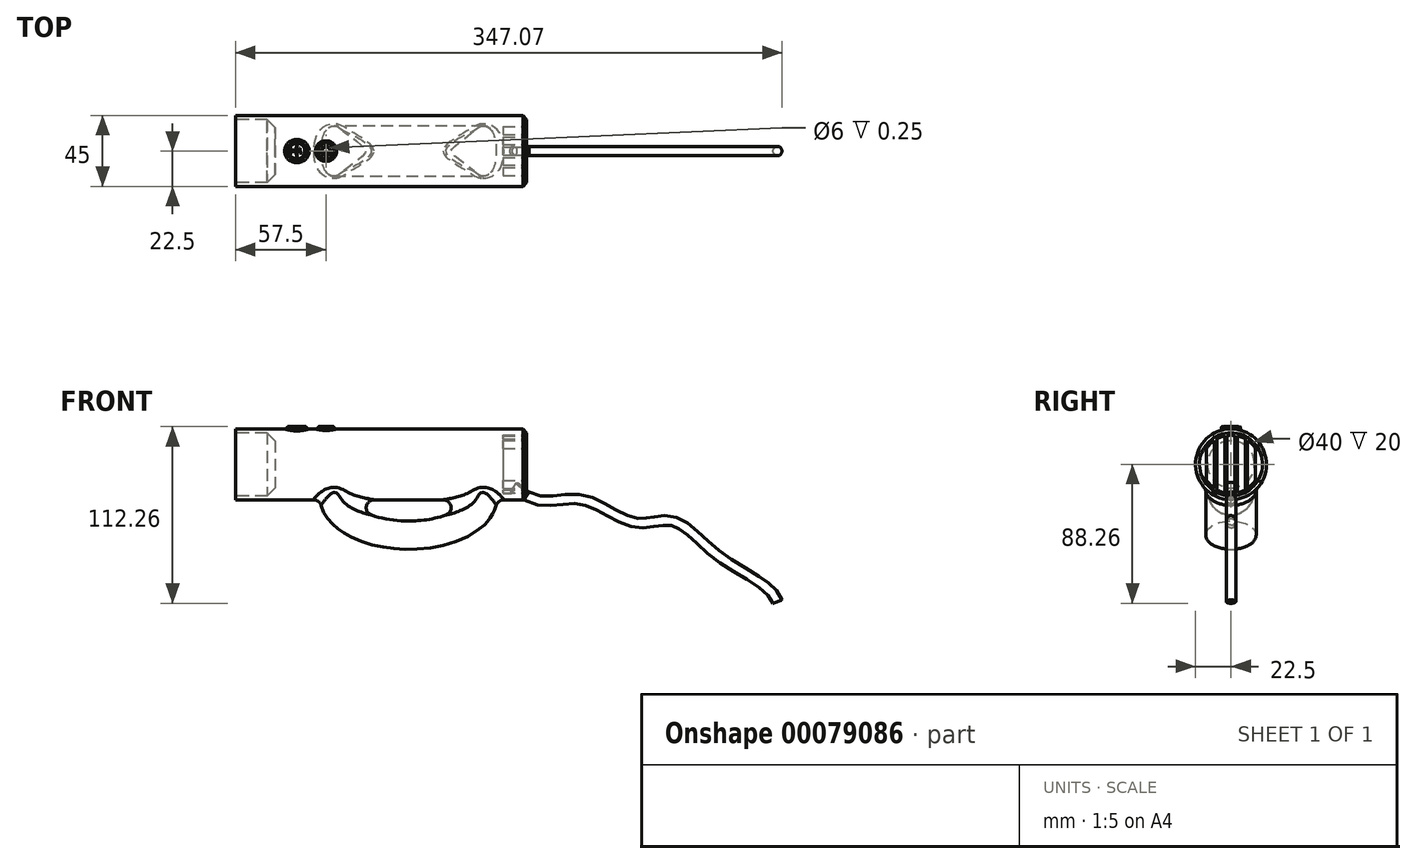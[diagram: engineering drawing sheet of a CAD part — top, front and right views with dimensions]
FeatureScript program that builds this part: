
annotation { "Feature Type Name" : "Feature", "Feature Type Description" : "" }
export const myFeature = defineFeature(function(context is Context, id is Id, definition is map)
    precondition{}
    {
        {
            var Q0;
            Q0=qCreatedBy(makeId("Front.planeOp"),FACE);
            var sketch = newSketch(context, id + "F0", { "sketchPlane" : qUnion([Q0])});
            skEllipse(sketch, "E0", {"center": v(0, -5) * mm, "majorRadius": 47.5 * mm, "minorRadius": 25 * mm, "majorAxis": v(1, 0)});
            skSolve(sketch);
        }
        {
            var Q0;
            Q0=qCreatedBy(makeId("Right.planeOp"),FACE);
            var sketch = newSketch(context, id + "F1", { "sketchPlane" : qUnion([Q0])});
            skLineSegment(sketch, "E1.0", {"start": v(0, -30) * mm, "end": v(0, 20) * mm});
            skEllipse(sketch, "E2", {"center": v(0, -30) * mm, "majorRadius": 16 * mm, "minorRadius": 9 * mm, "majorAxis": v(-1, 0)});
            skSolve(sketch);
        }
        {
            var Q0;
            Q0=makeQuery(id+"F1.imprint","IMPRINT",FACE,{"disambiguationData":[TD([[makeQuery(id+"F1.imprint","IMPRINT",EDGE,{"derivedFrom":sQuery(id+"F1.wireOp",EDGE,"E2")}),1.0]])]});
            var Q1;
            Q1=sQuery(id+"F0.wireOp",EDGE,"E0");
            sweep(context, id + "F2", {"profiles" : qUnion([Q0]), "path" : qUnion([Q1])});
        }
        {
            var Q0;
            Q0=qCreatedBy(makeId("Right.planeOp"),FACE);
            var sketch = newSketch(context, id + "F3", { "sketchPlane" : qUnion([Q0])});
            skCircle(sketch, "E3", {"center": v(0, 15) * mm, "radius": 22.5 * mm});
            skSolve(sketch);
        }
        {
            var Q0;
            Q0=makeQuery(id+"F3.imprint","IMPRINT",FACE,{"disambiguationData":[TD([[makeQuery(id+"F3.imprint","IMPRINT",EDGE,{"derivedFrom":sQuery(id+"F3.wireOp",EDGE,"E3")}),1.0]])]});
            extrude(context, id + "F4", {"entities" : qUnion([Q0]), "depth" : 75 * mm, "hasSecondDirection" : true, "secondDirectionOppositeDirection" : true, "secondDirectionDepth" : 110 * mm});
        }
        {
            var Q0;
            Q0=makeQuery(id+"F4.opExtrude","CAP_FACE",FACE,{"disambiguationData":[OSD([sQuery(id+"F3.wireOp",EDGE,"E3")])],"isStart":true});
            var sketch = newSketch(context, id + "F5", { "sketchPlane" : qUnion([Q0])});
            skCircle(sketch, "E4", {"center": v(0, 15) * mm, "radius": 20 * mm});
            skSolve(sketch);
        }
        {
            var Q0;
            Q0=makeQuery(id+"F5.imprint","IMPRINT",FACE,{"disambiguationData":[TD([[makeQuery(id+"F5.imprint","IMPRINT",EDGE,{"derivedFrom":sQuery(id+"F5.wireOp",EDGE,"E4")}),1.0]])]});
            extrude(context, id + "F6", {"entities" : qUnion([Q0]), "operationType" : NewBodyOperationType.REMOVE, "oppositeDirection" : true, "depth" : 25 * mm});
        }
        {
            var Q0;
            Q0=makeQuery(id+"F4.opExtrude","SWEPT_BODY",BODY,{"disambiguationData":[OSD([sQuery(id+"F3.wireOp",EDGE,"E3")])]});
            var Q1;
            Q1=makeQuery(id+"F2.opSweep","SWEPT_BODY",BODY,{"disambiguationData":[OSD([sQuery(id+"F0.wireOp",EDGE,"E0"),sQuery(id+"F1.wireOp",EDGE,"E2")])]});
            booleanBodies(context, id + "F7", {"operationType" : BooleanOperationType.UNION, "tools" : qUnion([Q0, Q1])});
        }
        {
            var Q0;
            Q0=makeQuery(id+"F7.opBoolean","INTERSECT",EDGE,{"disambiguationData":[OD(0.0)],"derivedFrom":[makeQuery(id+"F2.opSweep","SWEPT_FACE",FACE,{"disambiguationData":[OSD([sQuery(id+"F0.wireOp",EDGE,"E0"),sQuery(id+"F1.wireOp",EDGE,"E2")])]}),makeQuery(id+"F4.opExtrude","SWEPT_FACE",FACE,{"disambiguationData":[OSD([sQuery(id+"F3.wireOp",EDGE,"E3")])]})]});
            var Q1;
            Q1=makeQuery(id+"F7.opBoolean","INTERSECT",EDGE,{"disambiguationData":[OD(1.0)],"derivedFrom":[makeQuery(id+"F2.opSweep","SWEPT_FACE",FACE,{"disambiguationData":[OSD([sQuery(id+"F0.wireOp",EDGE,"E0"),sQuery(id+"F1.wireOp",EDGE,"E2")])]}),makeQuery(id+"F4.opExtrude","SWEPT_FACE",FACE,{"disambiguationData":[OSD([sQuery(id+"F3.wireOp",EDGE,"E3")])]})]});
            fillet(context, id + "F8", {"entities" : qUnion([Q0, Q1]), "radius" : 5 * mm, "tangentPropagation" : true, "allowEdgeOverflow" : false});
        }
        {
            var Q0;
            Q0=makeQuery(id+"F4.opExtrude","CAP_EDGE",EDGE,{"disambiguationData":[OSD([sQuery(id+"F3.wireOp",EDGE,"E3")])],"isStart":false});
            chamfer(context, id + "F9", {"entities" : qUnion([Q0]), "width" : 2.5 * mm, "tangentPropagation" : true});
        }
        {
            var Q0;
            Q0=qCreatedBy(makeId("Top.planeOp"),FACE);
            var sketch = newSketch(context, id + "F10", { "sketchPlane" : qUnion([Q0])});
            skCircle(sketch, "E5", {"center": v(-52.5, 0) * mm, "radius": 5 * mm});
            skCircle(sketch, "E6", {"center": v(-71, 0) * mm, "radius": 6 * mm});
            skSolve(sketch);
        }
        {
            var Q0;
            Q0=makeQuery(id+"F10.imprint","IMPRINT",FACE,{"disambiguationData":[TD([[makeQuery(id+"F10.imprint","IMPRINT",EDGE,{"derivedFrom":sQuery(id+"F10.wireOp",EDGE,"E5")}),1.0]])]});
            var Q1;
            Q1=makeQuery(id+"F10.imprint","IMPRINT",FACE,{"disambiguationData":[TD([[makeQuery(id+"F10.imprint","IMPRINT",EDGE,{"derivedFrom":sQuery(id+"F10.wireOp",EDGE,"E6")}),1.0]])]});
            extrude(context, id + "F11", {"entities" : qUnion([Q0, Q1]), "depth" : 39 * mm, "hasSecondDirection" : true, "secondDirectionOppositeDirection" : false, "secondDirectionDepth" : 25 * mm});
        }
        {
            var Q0;
            Q0=makeQuery(id+"F11.opExtrude","CAP_EDGE",EDGE,{"disambiguationData":[OSD([sQuery(id+"F10.wireOp",EDGE,"E6")])],"isStart":false});
            var Q1;
            Q1=makeQuery(id+"F11.opExtrude","CAP_FACE",FACE,{"disambiguationData":[OSD([sQuery(id+"F10.wireOp",EDGE,"E5")])],"isStart":false});
            fillet(context, id + "F12", {"entities" : qUnion([Q0, Q1]), "radius" : 0.5 * mm, "tangentPropagation" : true, "allowEdgeOverflow" : false});
        }
        {
            var Q0;
            Q0=makeQuery(id+"F4.opExtrude","SWEPT_BODY",BODY,{"disambiguationData":[OSD([sQuery(id+"F3.wireOp",EDGE,"E3")])]});
            var Q1;
            Q1=makeQuery(id+"F11.opExtrude","SWEPT_BODY",BODY,{"disambiguationData":[OSD([sQuery(id+"F10.wireOp",EDGE,"E6")])]});
            var Q2;
            Q2=makeQuery(id+"F11.opExtrude","SWEPT_BODY",BODY,{"disambiguationData":[OSD([sQuery(id+"F10.wireOp",EDGE,"E5")])]});
            booleanBodies(context, id + "F13", {"operationType" : BooleanOperationType.UNION, "tools" : qUnion([Q0, Q1, Q2])});
        }
        {
            var Q0;
            Q0=makeQuery(id+"F13.opBoolean","INTERSECT",EDGE,{"derivedFrom":[makeQuery(id+"F4.opExtrude","SWEPT_FACE",FACE,{"disambiguationData":[OSD([sQuery(id+"F3.wireOp",EDGE,"E3")])]}),makeQuery(id+"F11.opExtrude","SWEPT_FACE",FACE,{"disambiguationData":[OSD([sQuery(id+"F10.wireOp",EDGE,"E6")])]})]});
            var Q1;
            Q1=makeQuery(id+"F13.opBoolean","INTERSECT",EDGE,{"derivedFrom":[makeQuery(id+"F4.opExtrude","SWEPT_FACE",FACE,{"disambiguationData":[OSD([sQuery(id+"F3.wireOp",EDGE,"E3")])]}),makeQuery(id+"F11.opExtrude","SWEPT_FACE",FACE,{"disambiguationData":[OSD([sQuery(id+"F10.wireOp",EDGE,"E5")])]})]});
            fillet(context, id + "F14", {"entities" : qUnion([Q0, Q1]), "radius" : 2 * mm, "tangentPropagation" : true, "allowEdgeOverflow" : false});
        }
        {
            var Q0;
            Q0=makeQuery(id+"F11.opExtrude","CAP_FACE",FACE,{"disambiguationData":[OSD([sQuery(id+"F10.wireOp",EDGE,"E5")])],"isStart":false});
            var sketch = newSketch(context, id + "F15", { "sketchPlane" : qUnion([Q0])});
            skCircle(sketch, "E7", {"center": v(-52.5, 0) * mm, "radius": 3 * mm});
            skCircle(sketch, "E8.0", {"center": v(-52.5, 0) * mm, "radius": 2.5 * mm});
            skLineSegment(sketch, "E9.bottom", {"start": v(-52.75, -2.75) * mm, "end": v(-52.25, -2.75) * mm});
            skLineSegment(sketch, "E9.top", {"start": v(-52.75, -0.75) * mm, "end": v(-52.25, -0.75) * mm});
            skLineSegment(sketch, "E9.left", {"start": v(-52.75, -2.75) * mm, "end": v(-52.75, -0.75) * mm});
            skLineSegment(sketch, "E9.right", {"start": v(-52.25, -2.75) * mm, "end": v(-52.25, -0.75) * mm});
            skSolve(sketch);
        }
        {
            var Q0;
            Q0=makeQuery(id+"F15.imprint","IMPRINT",FACE,{"disambiguationData":[TD([[makeQuery(id+"F15.imprint","IMPRINT",EDGE,{"derivedFrom":sQuery(id+"F15.wireOp",EDGE,"E7")}),1.0]])]});
            var Q1;
            {var subQ5=sQuery(id+"F15.wireOp",EDGE,"E9.top");Q1=makeQuery(id+"F15.imprint","IMPRINT",FACE,{"disambiguationData":[TD([[makeQuery(id+"F15.imprint","IMPRINT",EDGE,{"derivedFrom":subQ5}),-1.0]])]});}
            var Q2;
            {var subQ5=sQuery(id+"F15.wireOp",EDGE,"E9.bottom");Q2=makeQuery(id+"F15.imprint","IMPRINT",FACE,{"disambiguationData":[TD([[makeQuery(id+"F15.imprint","IMPRINT",EDGE,{"derivedFrom":subQ5}),1.0]])]});}
            extrude(context, id + "F16", {"entities" : qUnion([Q0, Q1, Q2]), "operationType" : NewBodyOperationType.REMOVE, "oppositeDirection" : true, "depth" : 0.25 * mm});
        }
        {
            var Q0;
            Q0=makeQuery(id+"F11.opExtrude","CAP_FACE",FACE,{"disambiguationData":[OSD([sQuery(id+"F10.wireOp",EDGE,"E6")])],"isStart":false});
            var sketch = newSketch(context, id + "F17", { "sketchPlane" : qUnion([Q0])});
            skCircle(sketch, "E10", {"center": v(-71, 0) * mm, "radius": 5.25 * mm});
            skCircle(sketch, "E11.0", {"center": v(-71, 0) * mm, "radius": 5 * mm});
            skLineSegment(sketch, "E12", {"start": v(-71.13, -5) * mm, "end": v(-71.13, 5) * mm});
            skLineSegment(sketch, "E13", {"start": v(-70.88, -5) * mm, "end": v(-70.88, 5) * mm});
            skText(sketch, "E14", { "text": "H", "fontName": "OpenSans-Regular.ttf"});
            skText(sketch, "E15", { "text": "L", "fontName": "OpenSans-Regular.ttf"});
            const initialGuessF17  = {"E14": [-0.07476, -0.00138, 1, 0, 0.00291], "E15": [-0.06985, -0.00138, 1, 0, 0.00325]};
            skSetInitialGuess(sketch, initialGuessF17);
            skSolve(sketch);
        }
        {
            var Q0;
            {var subQ0=sQuery(id+"F17.wireOp",EDGE,"E12");Q0=makeQuery(id+"F17.imprint","IMPRINT",FACE,{"disambiguationData":[TD([[makeQuery(id+"F17.imprint","IMPRINT",EDGE,{"derivedFrom":subQ0}),1.0]])]});}
            var Q1;
            {var subQ0=sQuery(id+"F17.wireOp",EDGE,"E13");Q1=makeQuery(id+"F17.imprint","IMPRINT",FACE,{"disambiguationData":[TD([[makeQuery(id+"F17.imprint","IMPRINT",EDGE,{"derivedFrom":subQ0}),-1.0]])]});}
            extrude(context, id + "F18", {"entities" : qUnion([Q0, Q1]), "operationType" : NewBodyOperationType.REMOVE, "oppositeDirection" : true, "depth" : 0.25 * mm});
        }
        {
            var Q0;
            Q0=makeQuery(id+"F6.boolean.opBoolean","COPY",EDGE,{"derivedFrom":makeQuery(id+"F6.opExtrude","CAP_EDGE",EDGE,{"disambiguationData":[OSD([sQuery(id+"F5.wireOp",EDGE,"E4")])],"isStart":false})});
            chamfer(context, id + "F19", {"entities" : qUnion([Q0]), "width" : 5 * mm, "tangentPropagation" : true});
        }
        {
            var Q0;
            Q0=makeQuery(id+"F4.opExtrude","CAP_FACE",FACE,{"disambiguationData":[OSD([sQuery(id+"F3.wireOp",EDGE,"E3")])],"isStart":false});
            var sketch = newSketch(context, id + "F20", { "sketchPlane" : qUnion([Q0])});
            skCircle(sketch, "E16", {"center": v(0, 15) * mm, "radius": 19 * mm});
            skCircle(sketch, "E17.0", {"center": v(0, 15) * mm, "radius": 18.5 * mm});
            skLineSegment(sketch, "E18", {"start": v(-2.5, 33.33) * mm, "end": v(-2.5, -3.33) * mm});
            skLineSegment(sketch, "E19", {"start": v(-4, 33.06) * mm, "end": v(-4, -3.06) * mm});
            skLineSegment(sketch, "E20", {"start": v(-9, 31.16) * mm, "end": v(-9, -1.16) * mm});
            skLineSegment(sketch, "E21", {"start": v(-10.5, 30.23) * mm, "end": v(-10.5, -0.23) * mm});
            skLineSegment(sketch, "E22", {"start": v(-15.5, 25.1) * mm, "end": v(-15.5, 4.9) * mm});
            skLineSegment(sketch, "E23", {"start": v(0, 6.34) * mm, "end": v(0, 24.89) * mm});
            skLineSegment(sketch, "E24.MirrorCS", {"start": v(2.5, 33.33) * mm, "end": v(2.5, -3.33) * mm});
            skLineSegment(sketch, "E25.MirrorCS", {"start": v(4, 33.06) * mm, "end": v(4, -3.06) * mm});
            skLineSegment(sketch, "E26.MirrorCS", {"start": v(9, 31.16) * mm, "end": v(9, -1.16) * mm});
            skLineSegment(sketch, "E27.MirrorCS", {"start": v(10.5, 30.23) * mm, "end": v(10.5, -0.23) * mm});
            skLineSegment(sketch, "E28.MirrorCS", {"start": v(15.5, 25.1) * mm, "end": v(15.5, 4.9) * mm});
            skSolve(sketch);
        }
        {
            var Q0;
            {var subQ0=sQuery(id+"F20.wireOp",EDGE,"E21");Q0=makeQuery(id+"F20.imprint","IMPRINT",FACE,{"disambiguationData":[TD([[makeQuery(id+"F20.imprint","IMPRINT",EDGE,{"derivedFrom":subQ0}),-1.0]])]});}
            var Q1;
            {var subQ0=sQuery(id+"F20.wireOp",EDGE,"E19");Q1=makeQuery(id+"F20.imprint","IMPRINT",FACE,{"disambiguationData":[TD([[makeQuery(id+"F20.imprint","IMPRINT",EDGE,{"derivedFrom":subQ0}),-1.0]])]});}
            var Q2;
            {var subQ0=sQuery(id+"F20.wireOp",EDGE,"E18");Q2=makeQuery(id+"F20.imprint","IMPRINT",FACE,{"disambiguationData":[TD([[makeQuery(id+"F20.imprint","IMPRINT",EDGE,{"derivedFrom":subQ0}),1.0]])]});}
            var Q3;
            {var subQ0=sQuery(id+"F20.wireOp",EDGE,"E27.MirrorCS");Q3=makeQuery(id+"F20.imprint","IMPRINT",FACE,{"disambiguationData":[TD([[makeQuery(id+"F20.imprint","IMPRINT",EDGE,{"derivedFrom":subQ0}),1.0]])]});}
            var Q4;
            {var subQ0=sQuery(id+"F20.wireOp",EDGE,"E25.MirrorCS");Q4=makeQuery(id+"F20.imprint","IMPRINT",FACE,{"disambiguationData":[TD([[makeQuery(id+"F20.imprint","IMPRINT",EDGE,{"derivedFrom":subQ0}),1.0]])]});}
            extrude(context, id + "F21", {"entities" : qUnion([Q0, Q1, Q2, Q3, Q4]), "operationType" : NewBodyOperationType.REMOVE, "oppositeDirection" : true, "depth" : 15 * mm});
        }
        {
            var Q0;
            Q0=qCreatedBy(makeId("Front.planeOp"),FACE);
            var sketch = newSketch(context, id + "F22", { "sketchPlane" : qUnion([Q0])});
            skLineSegment(sketch, "E29.0", {"start": v(75, 35) * mm, "end": v(75, -5) * mm});
            skFitSpline(sketch, "E30", {"points": [v(75, -5) * mm, v(109.7, -7.3) * mm, v(143.25, -22.02) * mm, v(167.6, -20.98) * mm, v(197.07, -43.44) * mm, v(234.26, -72.2) * mm], "startDerivative": vector(166.8, -103.94) * mm, "endDerivative": vector(54.08, -144.7) * mm});
            skSolve(sketch);
        }
        {
            var Q0;
            Q0=sQuery(id+"F22.wireOp",VERTEX,"E30.end");
            var Q1;
            Q1=sQuery(id+"F22.wireOp",EDGE,"E30");
            cPlane(context, id + "F23", {"entities" : qUnion([Q0, Q1]), "cplaneType" : CPlaneType.CURVE_POINT, "offset" : 150 * mm, "width" : 150 * mm, "height" : 150 * mm});
        }
        {
            var Q0;
            Q0=qCreatedBy(id+"F23.planeOp",FACE);
            var sketch = newSketch(context, id + "F24", { "sketchPlane" : qUnion([Q0])});
            skPoint(sketch, "E31.0", {"position": v(194.15, 0) * mm});
            skCircle(sketch, "E32", {"center": v(194.15, 0) * mm, "radius": 3 * mm});
            skSolve(sketch);
        }
        {
            var Q0;
            Q0=makeQuery(id+"F24.imprint","IMPRINT",FACE,{"disambiguationData":[TD([[makeQuery(id+"F24.imprint","IMPRINT",EDGE,{"derivedFrom":sQuery(id+"F24.wireOp",EDGE,"E32")}),1.0]])]});
            var Q1;
            Q1=sQuery(id+"F22.wireOp",EDGE,"E30");
            sweep(context, id + "F25", {"profiles" : qUnion([Q0]), "path" : qUnion([Q1])});
        }
        {
            var Q0;
            Q0=makeQuery(id+"F25.opSweep","CAP_FACE",FACE,{"disambiguationData":[OSD([sQuery(id+"F22.wireOp",VERTEX,"E30.start"),sQuery(id+"F24.wireOp",EDGE,"E32")])],"isStart":false});
            extrude(context, id + "F26", {"entities" : qUnion([Q0]), "operationType" : NewBodyOperationType.ADD, "depth" : 10 * mm, "hasDraft" : true, "draftAngle" : 5 * degree});
        }
    });
